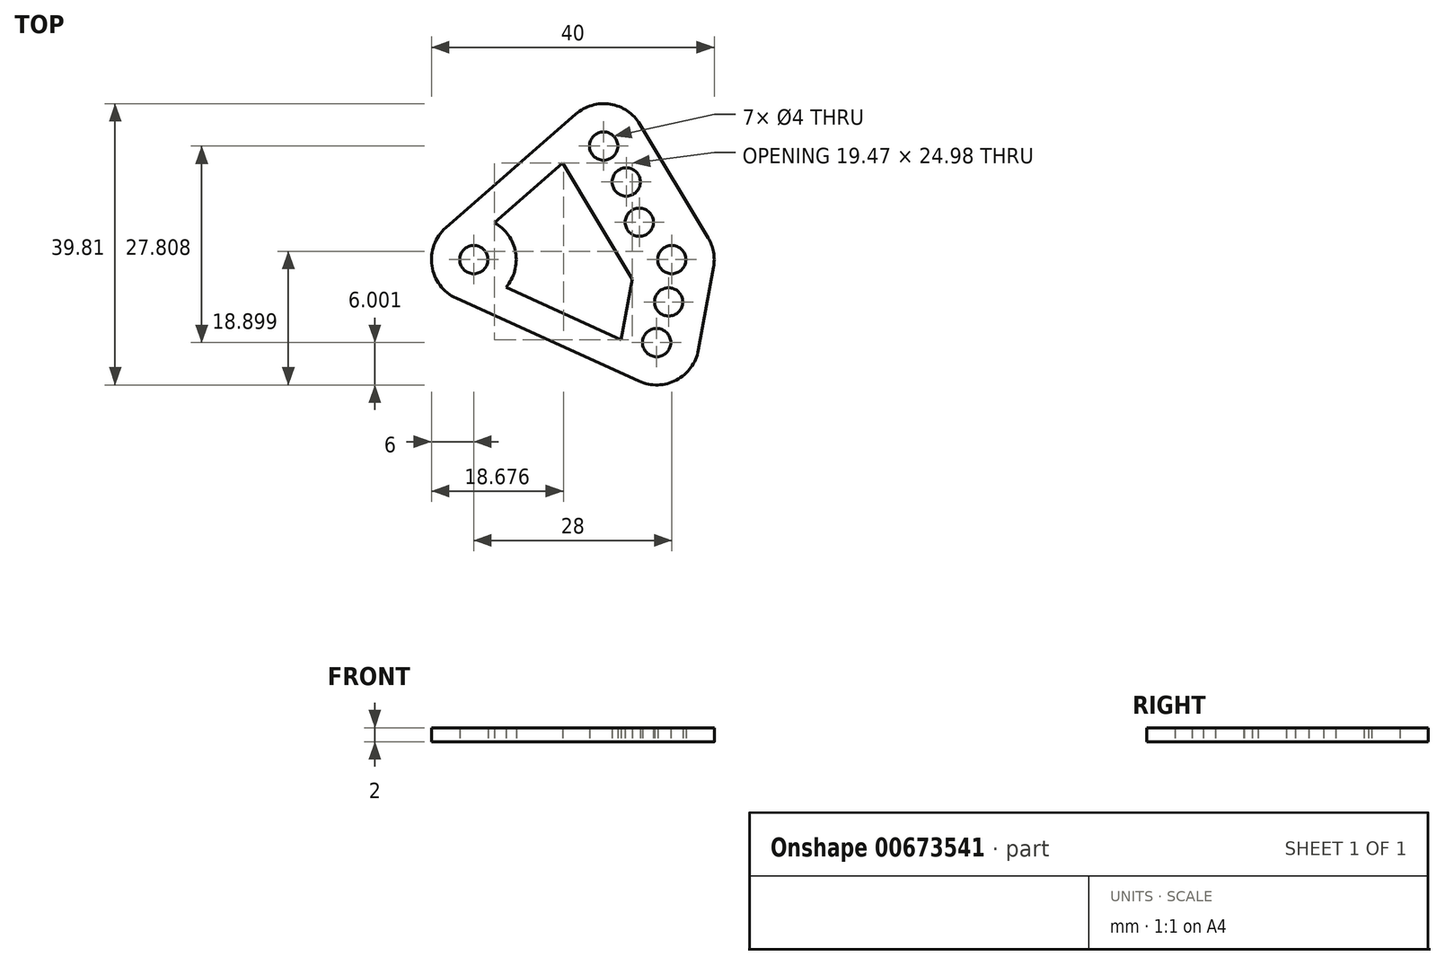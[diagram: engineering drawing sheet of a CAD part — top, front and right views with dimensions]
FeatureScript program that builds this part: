
annotation { "Feature Type Name" : "Feature", "Feature Type Description" : "" }
export const myFeature = defineFeature(function(context is Context, id is Id, definition is map)
    precondition{}
    {
        {
            var Q0;
            Q0=qCreatedBy(makeId("Top.planeOp"),FACE);
            var sketch = newSketch(context, id + "F0", { "sketchPlane" : qUnion([Q0])});
            skCircle(sketch, "E0", {"center": v(0, 0) * mm, "radius": 2 * mm});
            skCircle(sketch, "E1", {"center": v(23.41, 5.29) * mm, "radius": 2 * mm});
            skCircle(sketch, "E2", {"center": v(28, 0) * mm, "radius": 2 * mm});
            skArc(sketch, "E3", {"start": v(-3.95, 4.52) * mm, "mid": v(-5.94, -0.88) * mm, "end": v(-2.48, -5.46) * mm});
            skCircle(sketch, "E4", {"center": v(21.56, 11) * mm, "radius": 2 * mm});
            skCircle(sketch, "E5", {"center": v(18.36, 16.07) * mm, "radius": 2 * mm});
            skCircle(sketch, "E6", {"center": v(25.86, -11.74) * mm, "radius": 2 * mm});
            skCircle(sketch, "E7", {"center": v(27.56, -5.98) * mm, "radius": 2 * mm});
            skLineSegment(sketch, "E8", {"start": v(-3.95, 4.52) * mm, "end": v(14.4, 20.58) * mm});
            skArc(sketch, "E9", {"start": v(14.4, 20.58) * mm, "mid": v(19.3, 22) * mm, "end": v(23.5, 19.16) * mm});
            skArc(sketch, "E10", {"start": v(33.15, 3.09) * mm, "mid": v(33.9, 1.07) * mm, "end": v(33.9, -1.08) * mm});
            skArc(sketch, "E11", {"start": v(31.76, -12.81) * mm, "mid": v(28.64, -17.05) * mm, "end": v(23.38, -17.2) * mm});
            skLineSegment(sketch, "E12", {"start": v(-2.48, -5.46) * mm, "end": v(23.38, -17.2) * mm});
            skLineSegment(sketch, "E13", {"start": v(33.9, -1.08) * mm, "end": v(31.76, -12.81) * mm});
            skLineSegment(sketch, "E14", {"start": v(33.15, 3.09) * mm, "end": v(23.5, 19.16) * mm});
            skArc(sketch, "E15", {"start": v(2.94, 5.23) * mm, "mid": v(5.91, 1.03) * mm, "end": v(4.54, -3.93) * mm});
            skPoint(sketch, "E16.startSnap0", {"position": v(10.45, -11.33) * mm});
            skLineSegment(sketch, "E17", {"start": v(2.94, 5.23) * mm, "end": v(12.56, 13.65) * mm});
            skLineSegment(sketch, "E18", {"start": v(12.56, 13.65) * mm, "end": v(22.41, -2.77) * mm});
            skLineSegment(sketch, "E19", {"start": v(20.85, -11.33) * mm, "end": v(4.54, -3.93) * mm});
            skLineSegment(sketch, "E20", {"start": v(20.85, -11.33) * mm, "end": v(22.41, -2.77) * mm});
            skSolve(sketch);
        }
        {
            var Q0;
            Q0=makeQuery(id+"F0.imprint","IMPRINT",FACE,{"disambiguationData":[TD([[makeQuery(id+"F0.imprint","IMPRINT",EDGE,{"derivedFrom":sQuery(id+"F0.wireOp",EDGE,"E0")}),-1.0]])]});
            extrude(context, id + "F1", {"entities" : qUnion([Q0]), "depth" : 2 * mm, "offsetDistance" : 25 * mm});
        }
    });
